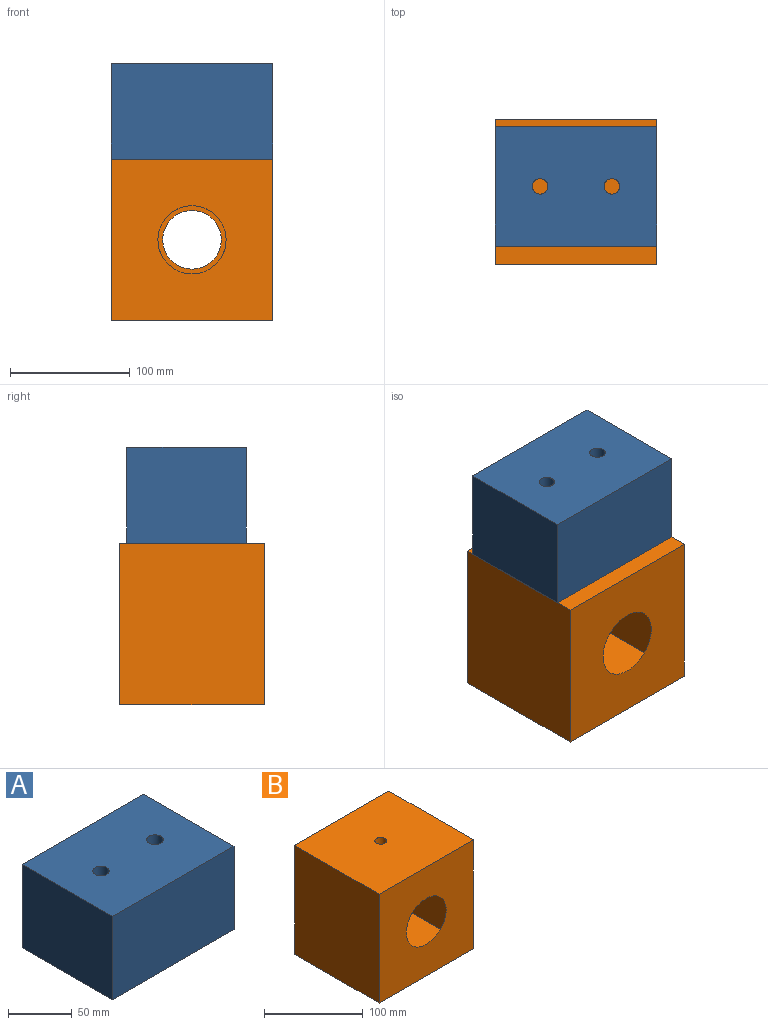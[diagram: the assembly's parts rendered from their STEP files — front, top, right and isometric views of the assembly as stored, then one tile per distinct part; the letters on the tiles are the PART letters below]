
ASSEMBLY  parts=2 mates=2
PART A: 13 faces, bbox 135x100x80 mm
  f0: plane 135x100mm, normal (0,0,-1), area 10993.1mm2, adj f1,f2,f3,f4,f6,f7,f8,f9
  f1: plane 135x80mm, normal (0,1,0), area 10800mm2, adj f0,f2,f4,f5
  f2: plane 100x80mm, normal (-1,0,0), area 8000mm2, adj f0,f1,f3,f5
  f3: plane 135x80mm, normal (0,-1,0), area 10800mm2, adj f0,f2,f4,f5
  f4: plane 100x80mm, normal (1,0,0), area 8000mm2, adj f0,f1,f3,f5
  f5: plane 135x100mm, normal (0,0,1), area 13234.5mm2, adj f1,f2,f3,f4,f11,f12
  f6: plane 60x10mm, normal (0,1,0), area 600mm2, adj f0,f7,f9,f10
  f7: cylinder r=15mm len=30mm, axis (0,0,-1), area 471.2mm2, adj f0,f6,f8,f10
  f8: plane 60x10mm, normal (0,-1,0), area 600mm2, adj f0,f7,f9,f10
  f9: cylinder r=15mm len=30mm, axis (0,0,-1), area 471.2mm2, adj f0,f6,f8,f10
  f10: plane 90x30mm, normal (0,0,-1), area 2241.4mm2, adj f6,f7,f8,f9,f11,f12
  f11: cylinder r=6.5mm len=70mm, axis (0,0,-1), area 2858.8mm2, adj f5,f10
  f12: cylinder r=6.5mm len=70mm, axis (0,0,-1), area 2858.8mm2, adj f5,f10
PART B: 10 faces, bbox 135x121x135 mm
  f0: cylinder r=24.5mm len=50mm, axis (0,-1,0), area 7696.9mm2, adj f1,f2
  f1: plane 135x135mm, normal (0,1,0), area 16339.3mm2, adj f0,f3,f4,f5,f6
  f2: plane 57x57mm, normal (0,-1,0), area 666mm2, adj f0,f7
  f3: plane 135x121mm, normal (0,0,1), area 16221.9mm2, adj f1,f4,f6,f8,f9
  f4: plane 135x121mm, normal (1,0,0), area 16335mm2, adj f1,f3,f5,f8
  f5: plane 135x121mm, normal (0,0,-1), area 16335mm2, adj f1,f4,f6,f8
  f6: plane 135x121mm, normal (-1,0,0), area 16335mm2, adj f1,f3,f5,f8
  f7: cylinder r=28.5mm len=71mm, axis (0,-1,0), area -12827.5mm2, adj f2,f8,f9
  f8: plane 135x135mm, normal (0,-1,0), area 15673.2mm2, adj f3,f4,f5,f6,f7
  f9: cylinder r=6mm len=39.64mm, axis (0,0,1), area 1482.3mm2, adj f3,f7
PLACE A t=(0,65,67.5)mm
PLACE B at identity fixed
MATE planar A.f0 <-> B.f3  axis (0,0,-1) through (0,65,67.5)mm
MATE planar A.f4 <-> B.f4  axis (1,0,0) through (67.5,115,147.5)mm
